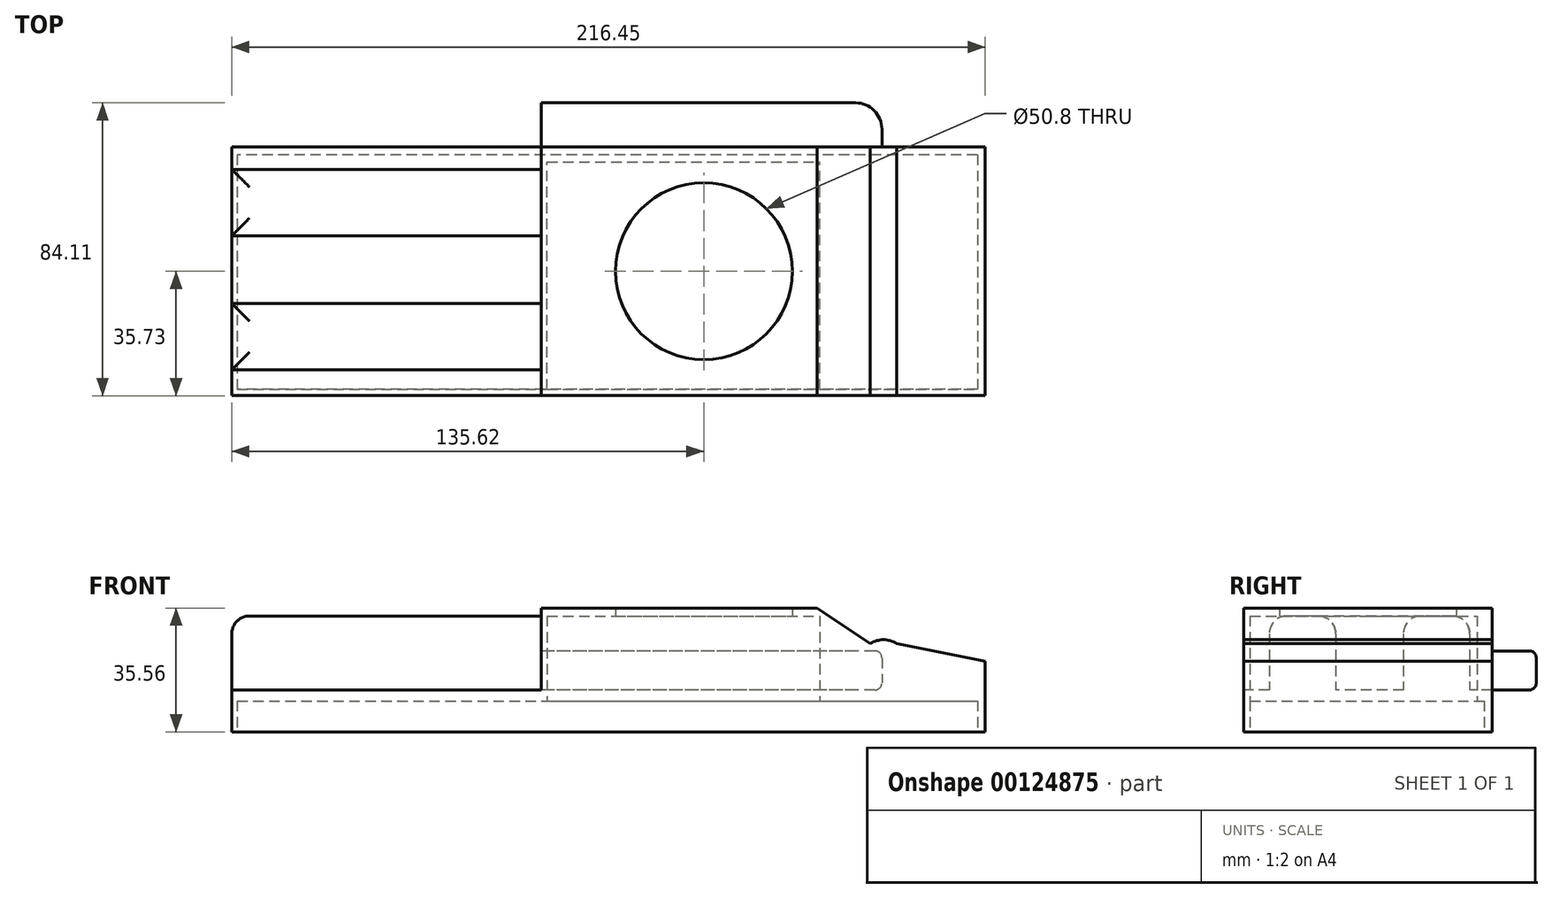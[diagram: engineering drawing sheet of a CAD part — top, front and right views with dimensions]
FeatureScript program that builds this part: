
annotation { "Feature Type Name" : "Feature", "Feature Type Description" : "" }
export const myFeature = defineFeature(function(context is Context, id is Id, definition is map)
    precondition{}
    {
        {
            var Q0;
            Q0=qCreatedBy(makeId("Top.planeOp"),FACE);
            var sketch = newSketch(context, id + "F0", { "sketchPlane" : qUnion([Q0])});
            skLineSegment(sketch, "E0.bottom", {"start": v(-46.72, 35.68) * mm, "end": v(47.8, 35.68) * mm});
            skLineSegment(sketch, "E0.top", {"start": v(-46.72, -35.73) * mm, "end": v(47.8, -35.73) * mm});
            skLineSegment(sketch, "E0.left", {"start": v(-46.72, 35.68) * mm, "end": v(-46.72, -35.73) * mm});
            skLineSegment(sketch, "E0.right", {"start": v(47.8, 35.68) * mm, "end": v(47.8, -35.73) * mm});
            skSolve(sketch);
        }
        {
            var Q0;
            Q0=makeQuery(id+"F0.imprint","IMPRINT",FACE,{"disambiguationData":[TD([[makeQuery(id+"F0.imprint","IMPRINT",EDGE,{"derivedFrom":sQuery(id+"F0.wireOp",EDGE,"E0.bottom")}),-1.0]])]});
            extrude(context, id + "F1", {"entities" : qUnion([Q0]), "depth" : 35.56 * mm});
        }
        {
            var Q0;
            Q0=qCreatedBy(makeId("Top.planeOp"),FACE);
            var sketch = newSketch(context, id + "F2", { "sketchPlane" : qUnion([Q0])});
            skCircle(sketch, "E1", {"center": v(0, 0) * mm, "radius": 25.4 * mm});
            skSolve(sketch);
        }
        {
            var Q0;
            Q0 = qSketchRegion(id + "F2", true);
            extrude(context, id + "F3", {"entities" : qUnion([Q0]), "operationType" : NewBodyOperationType.REMOVE, "depth" : 35.56 * mm});
        }
        {
            var Q0;
            Q0=makeQuery(id+"F1.opExtrude","CAP_EDGE",EDGE,{"disambiguationData":[OSD([sQuery(id+"F0.wireOp",EDGE,"E0.right")])],"isStart":false});
            chamfer(context, id + "F4", {"entities" : qUnion([Q0]), "chamferType" : ChamferType.TWO_OFFSETS, "width1" : 10.16 * mm, "oppositeDirection" : false, "width2" : 15.24 * mm, "tangentPropagation" : true});
        }
        {
            var Q0;
            Q0=makeQuery(id+"F1.opExtrude","SWEPT_FACE",FACE,{"disambiguationData":[OSD([sQuery(id+"F0.wireOp",EDGE,"E0.right")])]});
            extrude(context, id + "F5", {"entities" : qUnion([Q0]), "operationType" : NewBodyOperationType.ADD, "depth" : 7.62 * mm});
        }
        {
            var Q0;
            {var subQ0=sQuery(id+"F0.wireOp",EDGE,"E0.bottom");Q0=makeQuery(id+"F5.boolean.opBoolean","MERGE",FACE,{"derivedFrom":[makeQuery(id+"F1.opExtrude","SWEPT_FACE",FACE,{"disambiguationData":[OSD([subQ0])]}),makeQuery(id+"F5.opExtrude","SWEPT_FACE",FACE,{"disambiguationData":[OSD([subQ0,sQuery(id+"F0.wireOp",EDGE,"E0.right")])]})]});}
            var sketch = newSketch(context, id + "F6", { "sketchPlane" : qUnion([Q0])});
            skArc(sketch, "E2", {"start": v(-47.8, 25.4) * mm, "mid": v(-51.62, 26.47) * mm, "end": v(-55.43, 25.4) * mm});
            skSolve(sketch);
        }
        {
            var Q0;
            Q0=makeQuery(id+"F6.imprint","IMPRINT",FACE,{"disambiguationData":[TD([[makeQuery(id+"F6.imprint","IMPRINT",EDGE,{"derivedFrom":sQuery(id+"F6.wireOp",EDGE,"E2")}),1.0]])]});
            extrude(context, id + "F7", {"entities" : qUnion([Q0]), "operationType" : NewBodyOperationType.ADD, "oppositeDirection" : true, "depth" : 71.4 * mm});
        }
        {
            var Q0;
            Q0=makeQuery(id+"F5.opExtrude","CAP_FACE",FACE,{"disambiguationData":[OSD([sQuery(id+"F0.wireOp",EDGE,"E0.right")])],"isStart":false});
            extrude(context, id + "F8", {"entities" : qUnion([Q0]), "operationType" : NewBodyOperationType.ADD, "depth" : 25.4 * mm});
        }
        {
            var Q0;
            Q0=makeQuery(id+"F8.opExtrude","CAP_EDGE",EDGE,{"disambiguationData":[OSD([sQuery(id+"F0.wireOp",EDGE,"E0.bottom"),sQuery(id+"F0.wireOp",EDGE,"E0.right"),sQuery(id+"F6.wireOp",EDGE,"E2")])],"isStart":false});
            chamfer(context, id + "F9", {"entities" : qUnion([Q0]), "chamferType" : ChamferType.TWO_OFFSETS, "width1" : 5.08 * mm, "oppositeDirection" : false, "width2" : 25.4 * mm, "tangentPropagation" : true});
        }
        {
            var Q0;
            Q0=makeQuery(id+"F1.opExtrude","SWEPT_FACE",FACE,{"disambiguationData":[OSD([sQuery(id+"F0.wireOp",EDGE,"E0.left")])]});
            var sketch = newSketch(context, id + "F10", { "sketchPlane" : qUnion([Q0])});
            skLineSegment(sketch, "E3.bottom", {"start": v(-35.68, 12.04) * mm, "end": v(35.73, 12.04) * mm});
            skLineSegment(sketch, "E3.top", {"start": v(-35.68, 0) * mm, "end": v(35.73, 0) * mm});
            skLineSegment(sketch, "E3.left", {"start": v(-35.68, 12.04) * mm, "end": v(-35.68, 0) * mm});
            skLineSegment(sketch, "E3.right", {"start": v(35.73, 12.04) * mm, "end": v(35.73, 0) * mm});
            skSolve(sketch);
        }
        {
            var Q0;
            Q0 = qSketchRegion(id + "F10", true);
            extrude(context, id + "F11", {"entities" : qUnion([Q0]), "operationType" : NewBodyOperationType.ADD, "depth" : 88.9 * mm});
        }
        {
            var Q0;
            Q0=makeQuery(id+"F1.opExtrude","SWEPT_FACE",FACE,{"disambiguationData":[OSD([sQuery(id+"F0.wireOp",EDGE,"E0.left")])]});
            var sketch = newSketch(context, id + "F12", { "sketchPlane" : qUnion([Q0])});
            skLineSegment(sketch, "E4.bottom", {"start": v(-29.26, 33.31) * mm, "end": v(-10.21, 33.31) * mm});
            skLineSegment(sketch, "E4.top", {"start": v(-29.26, 12.04) * mm, "end": v(-10.21, 12.04) * mm});
            skLineSegment(sketch, "E4.left", {"start": v(-29.26, 33.31) * mm, "end": v(-29.26, 12.04) * mm});
            skLineSegment(sketch, "E4.right", {"start": v(-10.21, 33.31) * mm, "end": v(-10.21, 12.04) * mm});
            skSolve(sketch);
        }
        {
            var Q0;
            Q0=makeQuery(id+"F12.imprint","IMPRINT",FACE,{"disambiguationData":[TD([[makeQuery(id+"F12.imprint","IMPRINT",EDGE,{"derivedFrom":sQuery(id+"F12.wireOp",EDGE,"E4.bottom")}),-1.0]])]});
            extrude(context, id + "F13", {"entities" : qUnion([Q0]), "operationType" : NewBodyOperationType.ADD, "depth" : 88.9 * mm});
        }
        {
            var Q0;
            Q0=makeQuery(id+"F1.opExtrude","SWEPT_FACE",FACE,{"disambiguationData":[OSD([sQuery(id+"F0.wireOp",EDGE,"E0.left")])]});
            var sketch = newSketch(context, id + "F14", { "sketchPlane" : qUnion([Q0])});
            skLineSegment(sketch, "E5.bottom", {"start": v(9.25, 33.31) * mm, "end": v(28.3, 33.31) * mm});
            skLineSegment(sketch, "E5.top", {"start": v(9.25, 12.04) * mm, "end": v(28.3, 12.04) * mm});
            skLineSegment(sketch, "E5.left", {"start": v(9.25, 33.31) * mm, "end": v(9.25, 12.04) * mm});
            skLineSegment(sketch, "E5.right", {"start": v(28.3, 33.31) * mm, "end": v(28.3, 12.04) * mm});
            skSolve(sketch);
        }
        {
            var Q0;
            Q0=makeQuery(id+"F14.imprint","IMPRINT",FACE,{"disambiguationData":[TD([[makeQuery(id+"F14.imprint","IMPRINT",EDGE,{"derivedFrom":sQuery(id+"F14.wireOp",EDGE,"E5.bottom")}),-1.0]])]});
            extrude(context, id + "F15", {"entities" : qUnion([Q0]), "operationType" : NewBodyOperationType.ADD, "depth" : 88.9 * mm});
        }
        {
            var Q0;
            Q0=makeQuery(id+"F13.opExtrude","SWEPT_EDGE",EDGE,{"disambiguationData":[OSD([sQuery(id+"F12.wireOp",EDGE,"E4.bottom"),sQuery(id+"F12.wireOp",EDGE,"E4.left")])]});
            var Q1;
            Q1=makeQuery(id+"F13.opExtrude","SWEPT_EDGE",EDGE,{"disambiguationData":[OSD([sQuery(id+"F12.wireOp",EDGE,"E4.bottom"),sQuery(id+"F12.wireOp",EDGE,"E4.right")])]});
            var Q2;
            Q2=makeQuery(id+"F15.opExtrude","SWEPT_EDGE",EDGE,{"disambiguationData":[OSD([sQuery(id+"F14.wireOp",EDGE,"E5.bottom"),sQuery(id+"F14.wireOp",EDGE,"E5.left")])]});
            var Q3;
            Q3=makeQuery(id+"F15.opExtrude","SWEPT_EDGE",EDGE,{"disambiguationData":[OSD([sQuery(id+"F14.wireOp",EDGE,"E5.bottom"),sQuery(id+"F14.wireOp",EDGE,"E5.right")])]});
            var Q4;
            Q4=makeQuery(id+"F13.opExtrude","CAP_EDGE",EDGE,{"disambiguationData":[OSD([sQuery(id+"F12.wireOp",EDGE,"E4.bottom")])],"isStart":false});
            var Q5;
            Q5=makeQuery(id+"F15.opExtrude","CAP_EDGE",EDGE,{"disambiguationData":[OSD([sQuery(id+"F14.wireOp",EDGE,"E5.bottom")])],"isStart":false});
            fillet(context, id + "F16", {"entities" : qUnion([Q0, Q1, Q2, Q3, Q4, Q5]), "radius" : 5.08 * mm, "tangentPropagation" : true, "allowEdgeOverflow" : false});
        }
        {
            var Q0;
            {var subQ0=sQuery(id+"F0.wireOp",EDGE,"E0.right");var subQ1=sQuery(id+"F0.wireOp",EDGE,"E0.bottom");Q0=makeQuery(id+"F11.boolean.opBoolean","MERGE",FACE,{"derivedFrom":[makeQuery(id+"F8.boolean.opBoolean","MERGE",FACE,{"derivedFrom":[makeQuery(id+"F7.boolean.opBoolean","MERGE",FACE,{"derivedFrom":[makeQuery(id+"F5.boolean.opBoolean","MERGE",FACE,{"derivedFrom":[makeQuery(id+"F1.opExtrude","SWEPT_FACE",FACE,{"disambiguationData":[OSD([subQ1])]}),makeQuery(id+"F5.opExtrude","SWEPT_FACE",FACE,{"disambiguationData":[OSD([subQ1,subQ0])]})]}),makeQuery(id+"F7.opExtrude","CAP_FACE",FACE,{"disambiguationData":[OSD([subQ1,subQ0,sQuery(id+"F6.wireOp",EDGE,"E2")])],"isStart":true})]}),makeQuery(id+"F8.opExtrude","SWEPT_FACE",FACE,{"disambiguationData":[OSD([subQ1,subQ0])]})]}),makeQuery(id+"F11.opExtrude","SWEPT_FACE",FACE,{"disambiguationData":[OSD([sQuery(id+"F10.wireOp",EDGE,"E3.left")])]})]});}
            var sketch = newSketch(context, id + "F17", { "sketchPlane" : qUnion([Q0])});
            skLineSegment(sketch, "E6.bottom", {"start": v(-51.14, 23.28) * mm, "end": v(46.72, 23.28) * mm});
            skLineSegment(sketch, "E6.top", {"start": v(-51.14, 12.04) * mm, "end": v(46.72, 12.04) * mm});
            skLineSegment(sketch, "E6.left", {"start": v(-51.14, 23.28) * mm, "end": v(-51.14, 12.04) * mm});
            skLineSegment(sketch, "E6.right", {"start": v(46.72, 23.28) * mm, "end": v(46.72, 12.04) * mm});
            skSolve(sketch);
        }
        {
            var Q0;
            Q0 = qSketchRegion(id + "F17", true);
            extrude(context, id + "F18", {"entities" : qUnion([Q0]), "operationType" : NewBodyOperationType.ADD, "depth" : 12.7 * mm});
        }
        {
            var Q0;
            Q0=makeQuery(id+"F18.opExtrude","CAP_EDGE",EDGE,{"disambiguationData":[OSD([sQuery(id+"F17.wireOp",EDGE,"E6.left")])],"isStart":false});
            fillet(context, id + "F19", {"entities" : qUnion([Q0]), "radius" : 7.62 * mm, "tangentPropagation" : true, "allowEdgeOverflow" : false});
        }
        {
            var Q0;
            Q0=makeQuery(id+"F19.opFillet","BLEND_EDGE",EDGE,{"blendedFrom":[makeQuery(id+"F18.opExtrude","CAP_EDGE",EDGE,{"disambiguationData":[OSD([sQuery(id+"F17.wireOp",EDGE,"E6.left")])],"isStart":false}),makeQuery(id+"F18.opExtrude","SWEPT_FACE",FACE,{"disambiguationData":[OSD([sQuery(id+"F17.wireOp",EDGE,"E6.bottom")])]})],"blendedInto":[makeQuery(id+"F18.opExtrude","SWEPT_FACE",FACE,{"disambiguationData":[OSD([sQuery(id+"F17.wireOp",EDGE,"E6.bottom")])]})]});
            var Q1;
            Q1=makeQuery(id+"F18.opExtrude","SWEPT_EDGE",EDGE,{"disambiguationData":[OSD([sQuery(id+"F17.wireOp",EDGE,"E6.bottom"),sQuery(id+"F17.wireOp",EDGE,"E6.left")])]});
            var Q2;
            Q2=makeQuery(id+"F18.opExtrude","CAP_EDGE",EDGE,{"disambiguationData":[OSD([sQuery(id+"F17.wireOp",EDGE,"E6.bottom")])],"isStart":false});
            var Q3;
            Q3=makeQuery(id+"F18.opExtrude","SWEPT_EDGE",EDGE,{"disambiguationData":[OSD([sQuery(id+"F17.wireOp",EDGE,"E6.top"),sQuery(id+"F17.wireOp",EDGE,"E6.left")])]});
            var Q4;
            Q4=makeQuery(id+"F19.opFillet","BLEND_EDGE",EDGE,{"blendedFrom":[makeQuery(id+"F18.opExtrude","CAP_EDGE",EDGE,{"disambiguationData":[OSD([sQuery(id+"F17.wireOp",EDGE,"E6.left")])],"isStart":false}),makeQuery(id+"F18.opExtrude","SWEPT_FACE",FACE,{"disambiguationData":[OSD([sQuery(id+"F17.wireOp",EDGE,"E6.top")])]})],"blendedInto":[makeQuery(id+"F18.opExtrude","SWEPT_FACE",FACE,{"disambiguationData":[OSD([sQuery(id+"F17.wireOp",EDGE,"E6.top")])]})]});
            var Q5;
            Q5=makeQuery(id+"F18.opExtrude","CAP_EDGE",EDGE,{"disambiguationData":[OSD([sQuery(id+"F17.wireOp",EDGE,"E6.top")])],"isStart":false});
            fillet(context, id + "F20", {"entities" : qUnion([Q0, Q1, Q2, Q3, Q4, Q5]), "radius" : 2.03 * mm, "tangentPropagation" : true, "allowEdgeOverflow" : false});
        }
        {
            var Q0;
            {var subQ0=sQuery(id+"F0.wireOp",EDGE,"E0.right");Q0=makeQuery(id+"F11.boolean.opBoolean","MERGE",FACE,{"derivedFrom":[makeQuery(id+"F8.boolean.opBoolean","MERGE",FACE,{"derivedFrom":[makeQuery(id+"F5.boolean.opBoolean","MERGE",FACE,{"derivedFrom":[makeQuery(id+"F1.opExtrude","CAP_FACE",FACE,{"disambiguationData":[OSD([sQuery(id+"F0.wireOp",EDGE,"E0.bottom"),sQuery(id+"F0.wireOp",EDGE,"E0.top"),sQuery(id+"F0.wireOp",EDGE,"E0.left"),subQ0])],"isStart":true}),makeQuery(id+"F5.opExtrude","SWEPT_FACE",FACE,{"disambiguationData":[OSD([subQ0]),TDD([makeQuery(id+"F1.opExtrude","CAP_EDGE",EDGE,{"disambiguationData":[OSD([subQ0])],"isStart":true})])]})]}),makeQuery(id+"F8.opExtrude","SWEPT_FACE",FACE,{"disambiguationData":[OSD([subQ0])]})]}),makeQuery(id+"F11.opExtrude","SWEPT_FACE",FACE,{"disambiguationData":[OSD([sQuery(id+"F10.wireOp",EDGE,"E3.top")])]})]});}
            var sketch = newSketch(context, id + "F21", { "sketchPlane" : qUnion([Q0])});
            skLineSegment(sketch, "E7.bottom", {"start": v(-134.06, 33.9) * mm, "end": v(78.58, 33.9) * mm});
            skLineSegment(sketch, "E7.top", {"start": v(-134.06, -33.47) * mm, "end": v(78.58, -33.47) * mm});
            skLineSegment(sketch, "E7.left", {"start": v(-134.06, 33.9) * mm, "end": v(-134.06, -33.47) * mm});
            skLineSegment(sketch, "E7.right", {"start": v(78.58, 33.9) * mm, "end": v(78.58, -33.47) * mm});
            skSolve(sketch);
        }
        {
            var Q0;
            Q0 = qSketchRegion(id + "F21", true);
            extrude(context, id + "F22", {"entities" : qUnion([Q0]), "operationType" : NewBodyOperationType.REMOVE, "endBound" : BoundingType.SYMMETRIC, "oppositeDirection" : true, "depth" : 17.78 * mm});
        }
        {
            var Q0;
            Q0=makeQuery(id+"F22.boolean.opBoolean","COPY",FACE,{"derivedFrom":makeQuery(id+"F22.opExtrude","CAP_FACE",FACE,{"disambiguationData":[OSD([sQuery(id+"F21.wireOp",EDGE,"E7.bottom"),sQuery(id+"F21.wireOp",EDGE,"E7.top"),sQuery(id+"F21.wireOp",EDGE,"E7.left"),sQuery(id+"F21.wireOp",EDGE,"E7.right")])],"isStart":false})});
            var sketch = newSketch(context, id + "F23", { "sketchPlane" : qUnion([Q0])});
            skLineSegment(sketch, "E8.bottom", {"start": v(-45.04, 33.9) * mm, "end": v(33.3, 33.9) * mm});
            skLineSegment(sketch, "E8.top", {"start": v(-45.04, -31.33) * mm, "end": v(33.3, -31.33) * mm});
            skLineSegment(sketch, "E8.left", {"start": v(-45.04, 33.9) * mm, "end": v(-45.04, -31.33) * mm});
            skLineSegment(sketch, "E8.right", {"start": v(33.3, 33.9) * mm, "end": v(33.3, -31.33) * mm});
            skSolve(sketch);
        }
        {
            var Q0;
            Q0 = qSketchRegion(id + "F23", true);
            extrude(context, id + "F24", {"entities" : qUnion([Q0]), "operationType" : NewBodyOperationType.REMOVE, "oppositeDirection" : true, "depth" : 24.38 * mm});
        }
    });
